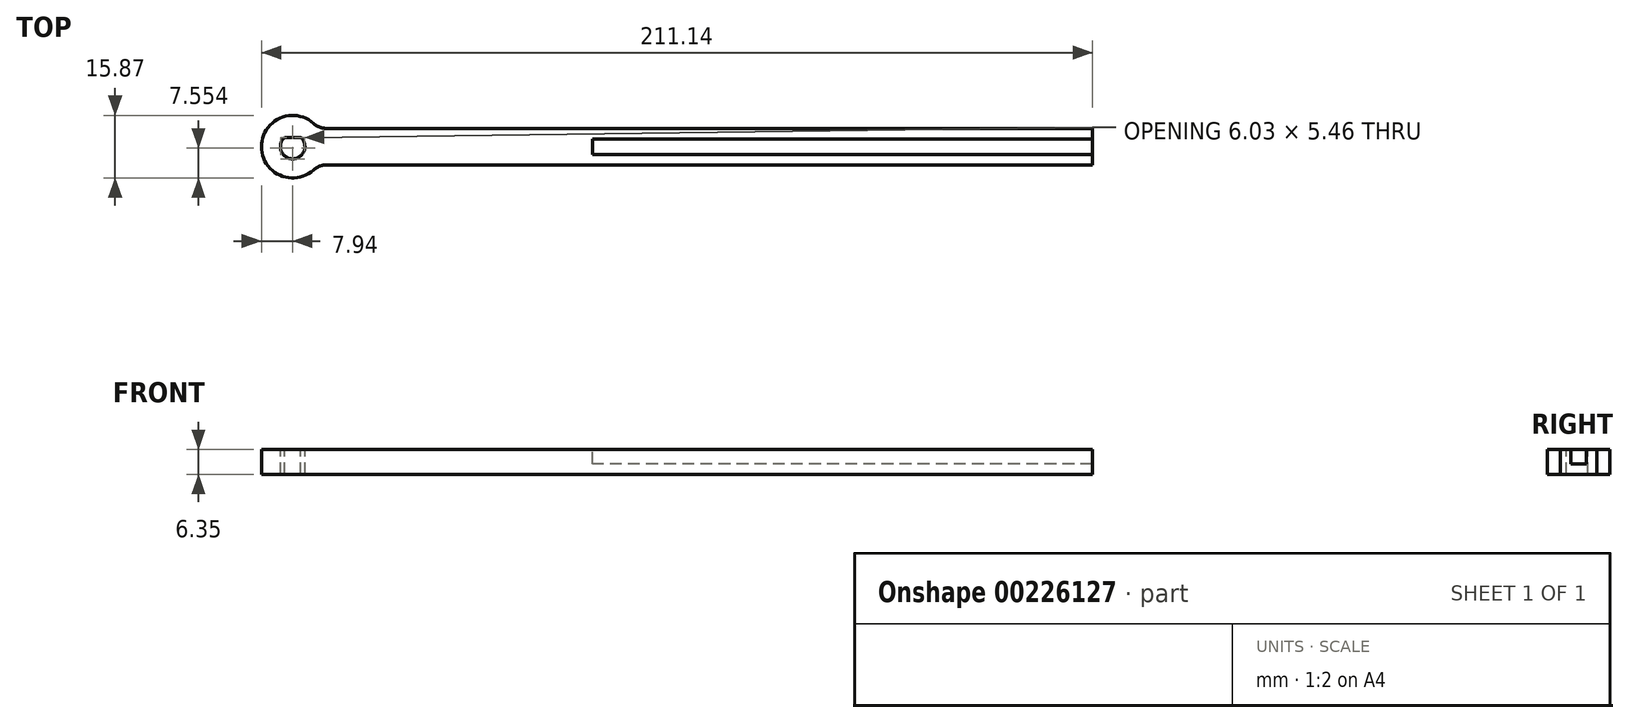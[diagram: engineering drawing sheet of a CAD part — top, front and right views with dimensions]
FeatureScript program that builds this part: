
annotation { "Feature Type Name" : "Feature", "Feature Type Description" : "" }
export const myFeature = defineFeature(function(context is Context, id is Id, definition is map)
    precondition{}
    {
        {
            var Q0;
            Q0=qCreatedBy(makeId("Top.planeOp"),FACE);
            var sketch = newSketch(context, id + "F0", { "sketchPlane" : qUnion([Q0])});
            skLineSegment(sketch, "E0.bottom", {"start": v(0, 0) * mm, "end": v(203.2, 0) * mm});
            skLineSegment(sketch, "E0.top", {"start": v(0, 9.27) * mm, "end": v(203.2, 9.27) * mm});
            skLineSegment(sketch, "E0.left", {"start": v(0, 0) * mm, "end": v(0, 9.27) * mm});
            skLineSegment(sketch, "E0.right", {"start": v(203.2, 0) * mm, "end": v(203.2, 9.27) * mm});
            skSolve(sketch);
        }
        {
            var Q0;
            Q0 = qSketchRegion(id + "F0", true);
            extrude(context, id + "F1", {"entities" : qUnion([Q0]), "depth" : 6.35 * mm});
        }
        {
            var Q0;
            Q0=makeQuery(id+"F1.opExtrude","CAP_FACE",FACE,{"disambiguationData":[OSD([sQuery(id+"F0.wireOp",EDGE,"E0.bottom"),sQuery(id+"F0.wireOp",EDGE,"E0.top"),sQuery(id+"F0.wireOp",EDGE,"E0.left"),sQuery(id+"F0.wireOp",EDGE,"E0.right")])],"isStart":false});
            var sketch = newSketch(context, id + "F2", { "sketchPlane" : qUnion([Q0])});
            skLineSegment(sketch, "E1.bottom", {"start": v(203.2, 6.6) * mm, "end": v(76.2, 6.6) * mm});
            skLineSegment(sketch, "E1.top", {"start": v(203.2, 2.67) * mm, "end": v(76.2, 2.67) * mm});
            skLineSegment(sketch, "E1.left", {"start": v(203.2, 6.6) * mm, "end": v(203.2, 2.67) * mm});
            skLineSegment(sketch, "E1.right", {"start": v(76.2, 6.6) * mm, "end": v(76.2, 2.67) * mm});
            skSolve(sketch);
        }
        {
            var Q0;
            Q0 = qSketchRegion(id + "F2", true);
            extrude(context, id + "F3", {"entities" : qUnion([Q0]), "operationType" : NewBodyOperationType.REMOVE, "oppositeDirection" : true, "depth" : 3.68 * mm});
        }
        {
            var Q0;
            Q0=makeQuery(id+"F1.opExtrude","CAP_FACE",FACE,{"disambiguationData":[OSD([sQuery(id+"F0.wireOp",EDGE,"E0.bottom"),sQuery(id+"F0.wireOp",EDGE,"E0.top"),sQuery(id+"F0.wireOp",EDGE,"E0.left"),sQuery(id+"F0.wireOp",EDGE,"E0.right")])],"isStart":false});
            var sketch = newSketch(context, id + "F4", { "sketchPlane" : qUnion([Q0])});
            skCircle(sketch, "E2", {"center": v(0, 4.64) * mm, "radius": 7.94 * mm});
            skSolve(sketch);
        }
        {
            var Q0;
            Q0 = qSketchRegion(id + "F4", true);
            var Q1;
            Q1=makeQuery(id+"F1.opExtrude","CAP_FACE",FACE,{"disambiguationData":[OSD([sQuery(id+"F0.wireOp",EDGE,"E0.bottom"),sQuery(id+"F0.wireOp",EDGE,"E0.top"),sQuery(id+"F0.wireOp",EDGE,"E0.left"),sQuery(id+"F0.wireOp",EDGE,"E0.right")])],"isStart":true});
            extrude(context, id + "F5", {"entities" : qUnion([Q0]), "operationType" : NewBodyOperationType.ADD, "endBound" : BoundingType.UP_TO_SURFACE, "oppositeDirection" : true, "endBoundEntityFace" : qUnion([Q1]), "depth" : 25.4 * mm});
        }
        {
            var Q0;
            Q0=makeQuery(id+"F5.boolean.opBoolean","INTERSECT",EDGE,{"derivedFrom":[makeQuery(id+"F1.opExtrude","SWEPT_FACE",FACE,{"disambiguationData":[OSD([sQuery(id+"F0.wireOp",EDGE,"E0.top")])]}),makeQuery(id+"F5.opExtrude","SWEPT_FACE",FACE,{"disambiguationData":[OSD([sQuery(id+"F4.wireOp",EDGE,"E2")])]})]});
            var Q1;
            Q1=makeQuery(id+"F5.boolean.opBoolean","INTERSECT",EDGE,{"derivedFrom":[makeQuery(id+"F1.opExtrude","SWEPT_FACE",FACE,{"disambiguationData":[OSD([sQuery(id+"F0.wireOp",EDGE,"E0.bottom")])]}),makeQuery(id+"F5.opExtrude","SWEPT_FACE",FACE,{"disambiguationData":[OSD([sQuery(id+"F4.wireOp",EDGE,"E2")])]})]});
            fillet(context, id + "F6", {"entities" : qUnion([Q0, Q1]), "radius" : 5.08 * mm, "tangentPropagation" : true, "allowEdgeOverflow" : false});
        }
        {
            var Q0;
            Q0=makeQuery(id+"F5.boolean.opBoolean","MERGE",FACE,{"derivedFrom":[makeQuery(id+"F1.opExtrude","CAP_FACE",FACE,{"disambiguationData":[OSD([sQuery(id+"F0.wireOp",EDGE,"E0.bottom"),sQuery(id+"F0.wireOp",EDGE,"E0.top"),sQuery(id+"F0.wireOp",EDGE,"E0.left"),sQuery(id+"F0.wireOp",EDGE,"E0.right")])],"isStart":false}),makeQuery(id+"F5.opExtrude","CAP_FACE",FACE,{"disambiguationData":[OSD([sQuery(id+"F4.wireOp",EDGE,"E2")])],"isStart":true})]});
            var sketch = newSketch(context, id + "F7", { "sketchPlane" : qUnion([Q0])});
            skCircle(sketch, "E3", {"center": v(0, 4.64) * mm, "radius": 3.11 * mm});
            skSolve(sketch);
        }
        {
            var Q0;
            Q0 = qSketchRegion(id + "F7", true);
            extrude(context, id + "F8", {"entities" : qUnion([Q0]), "operationType" : NewBodyOperationType.REMOVE, "endBound" : BoundingType.THROUGH_ALL, "oppositeDirection" : true, "depth" : 25.4 * mm});
        }
        {
            var Q0;
            Q0=makeQuery(id+"F5.boolean.opBoolean","MERGE",FACE,{"derivedFrom":[makeQuery(id+"F1.opExtrude","CAP_FACE",FACE,{"disambiguationData":[OSD([sQuery(id+"F0.wireOp",EDGE,"E0.bottom"),sQuery(id+"F0.wireOp",EDGE,"E0.top"),sQuery(id+"F0.wireOp",EDGE,"E0.left"),sQuery(id+"F0.wireOp",EDGE,"E0.right")])],"isStart":false}),makeQuery(id+"F5.opExtrude","CAP_FACE",FACE,{"disambiguationData":[OSD([sQuery(id+"F4.wireOp",EDGE,"E2")])],"isStart":true})]});
            var sketch = newSketch(context, id + "F9", { "sketchPlane" : qUnion([Q0])});
            skLineSegment(sketch, "E4.bottom", {"start": v(-4.39, 10.16) * mm, "end": v(5.14, 10.16) * mm});
            skLineSegment(sketch, "E4.top", {"start": v(-4.39, 6.99) * mm, "end": v(5.14, 6.99) * mm});
            skLineSegment(sketch, "E4.left", {"start": v(-4.39, 10.16) * mm, "end": v(-4.39, 6.99) * mm});
            skLineSegment(sketch, "E4.right", {"start": v(5.14, 10.16) * mm, "end": v(5.14, 6.99) * mm});
            skSolve(sketch);
        }
        {
            var Q0;
            Q0 = qSketchRegion(id + "F9", true);
            var Q1;
            {var subQ0=sQuery(id+"F0.wireOp",EDGE,"E0.right");var subQ1=sQuery(id+"F0.wireOp",EDGE,"E0.left");var subQ2=sQuery(id+"F0.wireOp",EDGE,"E0.top");var subQ3=sQuery(id+"F0.wireOp",EDGE,"E0.bottom");Q1=makeQuery(id+"F5.boolean.opBoolean","MERGE",FACE,{"derivedFrom":[makeQuery(id+"F1.opExtrude","CAP_FACE",FACE,{"disambiguationData":[OSD([subQ3,subQ2,subQ1,subQ0])],"isStart":true}),makeQuery(id+"F5.opExtrude","CAP_FACE",FACE,{"disambiguationData":[OSD([subQ3,subQ2,subQ1,subQ0])],"isStart":false})]});}
            extrude(context, id + "F10", {"entities" : qUnion([Q0]), "operationType" : NewBodyOperationType.ADD, "endBound" : BoundingType.UP_TO_SURFACE, "oppositeDirection" : true, "endBoundEntityFace" : qUnion([Q1]), "depth" : 25.4 * mm});
        }
    });
